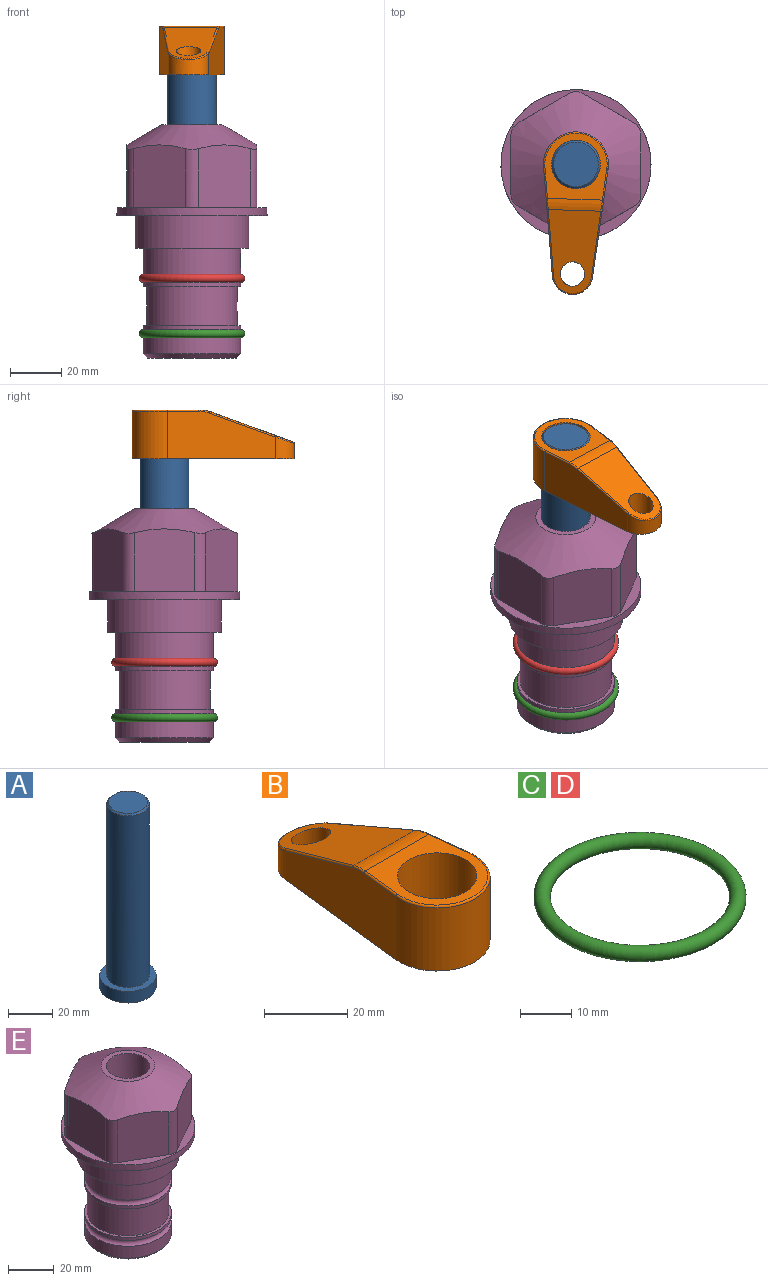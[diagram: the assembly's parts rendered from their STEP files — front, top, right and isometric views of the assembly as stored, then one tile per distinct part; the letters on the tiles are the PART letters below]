
ASSEMBLY  parts=5 mates=3
PART A: 6 faces, bbox 25.4x25.4x101.6 mm
  f0: plane 17.46x17.46mm, normal (0,0,1), area 239.5mm2, adj f5
  f1: plane 25.4x25.4mm, normal (0,0,-1), area 506.7mm2, adj f2
  f2: cylinder r=12.7mm len=25.4mm, axis (0,0,1), area 506.7mm2, adj f1,f3
  f3: plane 25.4x25.4mm, normal (0,0,1), area 221.7mm2, adj f2,f4
  f4: cylinder r=9.53mm len=94.46mm, axis (0,0,1), area 5653mm2, adj f3,f5
  f5: cone r=8.73mm half-angle=45deg, axis (0,0,-1), area 64.4mm2, adj f0,f4
PART B: 44 faces, bbox 27.5x64.5x19.1 mm
  f0: plane 2.3x0.95mm, normal (0,0,-1), area 1mm2, adj f25,f30,f34
  f1: plane 63.5x25.4mm, normal (0,0,-1), area 561.7mm2, adj f2,f3,f4,f5,f6,f7,f19,f20
  f2: cylinder r=12.7mm len=25.4mm, axis (0,0,-1), area 792.2mm2, adj f1,f3,f5,f13
  f3: plane 42.33x18.54mm, normal (0.99,0.11,0), area 647mm2, adj f1,f2,f4,f11,f12,f14
  f4: cylinder r=7.94mm len=15.78mm, axis (0,0,-1), area 158.6mm2, adj f1,f3,f5,f16
  f5: plane 42.33x18.54mm, normal (-0.99,0.11,0), area 647mm2, adj f1,f2,f4,f15,f17,f18
  f6: cylinder r=9.53mm len=19.05mm, axis (0,0,-1), area 1140.1mm2, adj f1,f8
  f7: cylinder r=4.76mm len=10.98mm, axis (0,0,-1), area 276.1mm2, adj f1,f9
  f8: plane 25.83x24.38mm, normal (0,0,1), area 262.2mm2, adj f6,f10,f11,f13,f15
  f9: plane 32.49x20.55mm, normal (0,0.34,0.94), area 489.9mm2, adj f7,f10,f14,f16,f18
  f10: cylinder r=12.7mm len=21.49mm, axis (-1,0,0), area 93.2mm2, adj f8,f9,f12,f17
  f11: cylinder r=0.51mm len=12.34mm, axis (0.11,-0.99,0), area 9.9mm2, adj f3,f8,f12,f13
  f12: bspline ~7.62x1.64mm, area 3.5mm2, adj f3,f10,f11,f14
  f13: torus R=12.19mm, axis (0,0,1), area 33.6mm2, adj f2,f8,f11,f15
  f14: cylinder r=0.51mm len=26.01mm, axis (0.1,-0.93,0.34), area 21.6mm2, adj f3,f9,f12,f16
  f15: cylinder r=0.51mm len=12.34mm, axis (0.11,0.99,0), area 9.9mm2, adj f5,f8,f13,f17
  f16: bspline ~15.78x7.05mm, area 15.7mm2, adj f4,f9,f14,f18
  f17: bspline ~7.62x1.64mm, area 3.5mm2, adj f5,f10,f15,f18
  f18: cylinder r=0.51mm len=26.01mm, axis (0.1,0.93,-0.34), area 21.6mm2, adj f5,f9,f16,f17
  f19: plane 21.6x14.29mm, normal (-0.99,-0.11,0), area 242.6mm2, adj f1,f26,f28,f34,f36,f38
  f20: plane 21.6x14.29mm, normal (0.99,-0.11,0), area 242.6mm2, adj f1,f27,f29,f37,f39,f41
  f21: cylinder r=12.7mm len=14.29mm, axis (0,0,-1), area 173.2mm2, adj f1,f26,f27,f30,f31,f33
  f22: cylinder r=7.94mm len=7.63mm, axis (0,0,-1), area 53.8mm2, adj f1,f28,f29,f42
  f23: plane 2.3x0.95mm, normal (0,0,-1), area 1mm2, adj f25,f33,f37
  f24: plane 17.94x12.32mm, normal (0,-0.34,-0.94), area 191.2mm2, adj f25,f38,f41,f42
  f25: cylinder r=9.53mm len=12.93mm, axis (-1,0,0), area 37.5mm2, adj f0,f23,f24,f31,f36,f39
  f26: cylinder r=1.59mm len=14.29mm, axis (0,0,-1), area 49mm2, adj f1,f19,f21,f32
  f27: cylinder r=1.59mm len=14.29mm, axis (0,0,-1), area 49mm2, adj f1,f20,f21,f35
  f28: cylinder r=1.59mm len=7.28mm, axis (0,0,-1), area 22.1mm2, adj f1,f19,f22,f40
  f29: cylinder r=1.59mm len=7.28mm, axis (0,0,-1), area 22.1mm2, adj f1,f20,f22,f43
  f30: torus R=14.29mm, axis (0,0,1), area 5.8mm2, adj f0,f21,f31,f32
  f31: bspline ~11.06x2.73mm, area 20.8mm2, adj f21,f25,f30,f33
  f32: sphere r=1.59mm, area 5.4mm2, adj f26,f30,f34
  f33: torus R=14.29mm, axis (0,0,1), area 5.8mm2, adj f21,f23,f31,f35
  f34: cylinder r=1.59mm len=1.68mm, axis (-0.11,0.99,0), area 2.4mm2, adj f0,f19,f32,f36
  f35: sphere r=1.59mm, area 5.4mm2, adj f27,f33,f37
  f36: bspline ~5.82x2.33mm, area 7.7mm2, adj f19,f25,f34,f38
  f37: cylinder r=1.59mm len=1.68mm, axis (0.11,0.99,0), area 2.4mm2, adj f20,f23,f35,f39
  f38: cylinder r=1.59mm len=18.33mm, axis (0.1,-0.93,0.34), area 46.7mm2, adj f19,f24,f36,f40
  f39: bspline ~5.82x2.33mm, area 7.7mm2, adj f20,f25,f37,f41
  f40: sphere r=1.59mm, area 3.6mm2, adj f28,f38,f42
  f41: cylinder r=1.59mm len=18.33mm, axis (0.1,0.93,-0.34), area 46.7mm2, adj f20,f24,f39,f43
  f42: bspline ~8.31x1.84mm, area 15.3mm2, adj f22,f24,f40,f43
  f43: sphere r=1.59mm, area 3.6mm2, adj f29,f41,f42
PART C: 1 faces, bbox 44.7x44.7x3.2 mm
  f0: torus R=19.05mm, axis (0,0,1), area 1193.9mm2
PART D: same geometry as C
PART E: 36 faces, bbox 58.7x58.7x91.2 mm
  f0: cylinder r=17.78mm len=35.56mm, axis (0,0,1), area 1670.8mm2, adj f23,f24,f31
  f1: cylinder r=19.05mm len=38.1mm, axis (0,0,1), area 1191.9mm2, adj f26,f27,f30
  f2: plane 58.66x58.66mm, normal (0,0,-1), area 1150.6mm2, adj f3,f28
  f3: cylinder r=29.33mm len=58.66mm, axis (0,0,-1), area 585.1mm2, adj f2,f4
  f4: plane 58.66x58.66mm, normal (0,0,1), area 475.9mm2, adj f3,f5,f6,f7,f8,f9,f10,f11
  f5: plane 24.5x20.32mm, normal (-0.5,0.87,0), area 562.8mm2, adj f4,f15,f16,f17
  f6: plane 24.5x20.32mm, normal (0.5,0.87,0), area 562.8mm2, adj f4,f14,f15,f17
  f7: plane 24.5x23.48mm, normal (1,0,0), area 562.8mm2, adj f4,f13,f14,f17
  f8: plane 24.5x20.32mm, normal (0.5,-0.87,0), area 562.8mm2, adj f4,f12,f13,f17
  f9: plane 24.5x20.32mm, normal (-0.5,-0.87,0), area 562.8mm2, adj f4,f11,f12,f17
  f10: plane 24.5x23.48mm, normal (-1,0,0), area 562.8mm2, adj f4,f11,f16,f17
  f11: cylinder r=5.08mm len=23.01mm, axis (0,0,-1), area 121.2mm2, adj f4,f9,f10,f17
  f12: cylinder r=5.08mm len=23.01mm, axis (0,0,-1), area 121.2mm2, adj f4,f8,f9,f17
  f13: cylinder r=5.08mm len=23.01mm, axis (0,0,-1), area 121.2mm2, adj f4,f7,f8,f17
  f14: cylinder r=5.08mm len=23.01mm, axis (0,0,-1), area 121.2mm2, adj f4,f6,f7,f17
  f15: cylinder r=5.08mm len=23.01mm, axis (0,0,-1), area 121.2mm2, adj f4,f5,f6,f17
  f16: cylinder r=5.08mm len=23.01mm, axis (0,0,-1), area 121.2mm2, adj f4,f5,f10,f17
  f17: cone r=11.73mm half-angle=60deg, axis (0,0,-1), area 2071.8mm2, adj f5,f6,f7,f8,f9,f10,f11,f12
  f18: plane 23.46x23.46mm, normal (0,0,1), area 147.4mm2, adj f17,f35
  f19: plane 34.93x34.93mm, normal (0,0,-1), area 958mm2, adj f29
  f20: cylinder r=19.05mm len=38.1mm, axis (0,0,1), area 760.1mm2, adj f21,f29
  f21: torus R=19.05mm, axis (0,0,1), area 565.3mm2, adj f20,f22
  f22: cylinder r=19.05mm len=38.1mm, axis (0,0,1), area 190mm2, adj f21,f23
  f23: plane 38.1x38.1mm, normal (0,0,1), area 146.9mm2, adj f0,f22
  f24: plane 38.1x38.1mm, normal (0,0,-1), area 146.9mm2, adj f0,f25
  f25: cylinder r=19.05mm len=38.1mm, axis (0,0,1), area 190mm2, adj f24,f26
  f26: torus R=19.05mm, axis (0,0,1), area 565.3mm2, adj f1,f25
  f27: plane 44.45x44.45mm, normal (0,0,-1), area 411.7mm2, adj f1,f28
  f28: cylinder r=22.23mm len=44.45mm, axis (0,0,1), area 1773.5mm2, adj f2,f27
  f29: cone r=19.05mm half-angle=45deg, axis (0,0,1), area 257.5mm2, adj f19,f20
  f30: cylinder r=3.17mm len=6.75mm, axis (-1,0,0), area 128mm2, adj f1,f33
  f31: cylinder r=3.17mm len=6.35mm, axis (-1,0,0), area 102.5mm2, adj f0,f33
  f32: plane 25.4x25.4mm, normal (0,0,1), area 506.7mm2, adj f33
  f33: cylinder r=12.7mm len=66.42mm, axis (0,0,-1), area 5236.2mm2, adj f30,f31,f32,f34
  f34: cone r=9.53mm half-angle=30deg, axis (0,0,-1), area 443.4mm2, adj f33,f35
  f35: cylinder r=9.53mm len=19.05mm, axis (0,0,-1), area 849mm2, adj f18,f34
PLACE A rot(axis=(0,0,-1),91.8deg) t=(0,0,0.46)mm
PLACE B rot(axis=(0,0,1),178.2deg) t=(0,0,55.07)mm
PLACE C t=(0,0,-21.59)mm
PLACE D at identity
PLACE E at identity fixed
MATE fastened C.f0 <-> E.f0  axis (0,0,1) through (0,0,-46.1)mm
MATE cylindrical A.f2 <-> E.f0  axis (0,0,1) through (0,0,26.1)mm
MATE fastened B.f2 <-> A.f2  axis (0,0,1) through (0,0,74.12)mm
